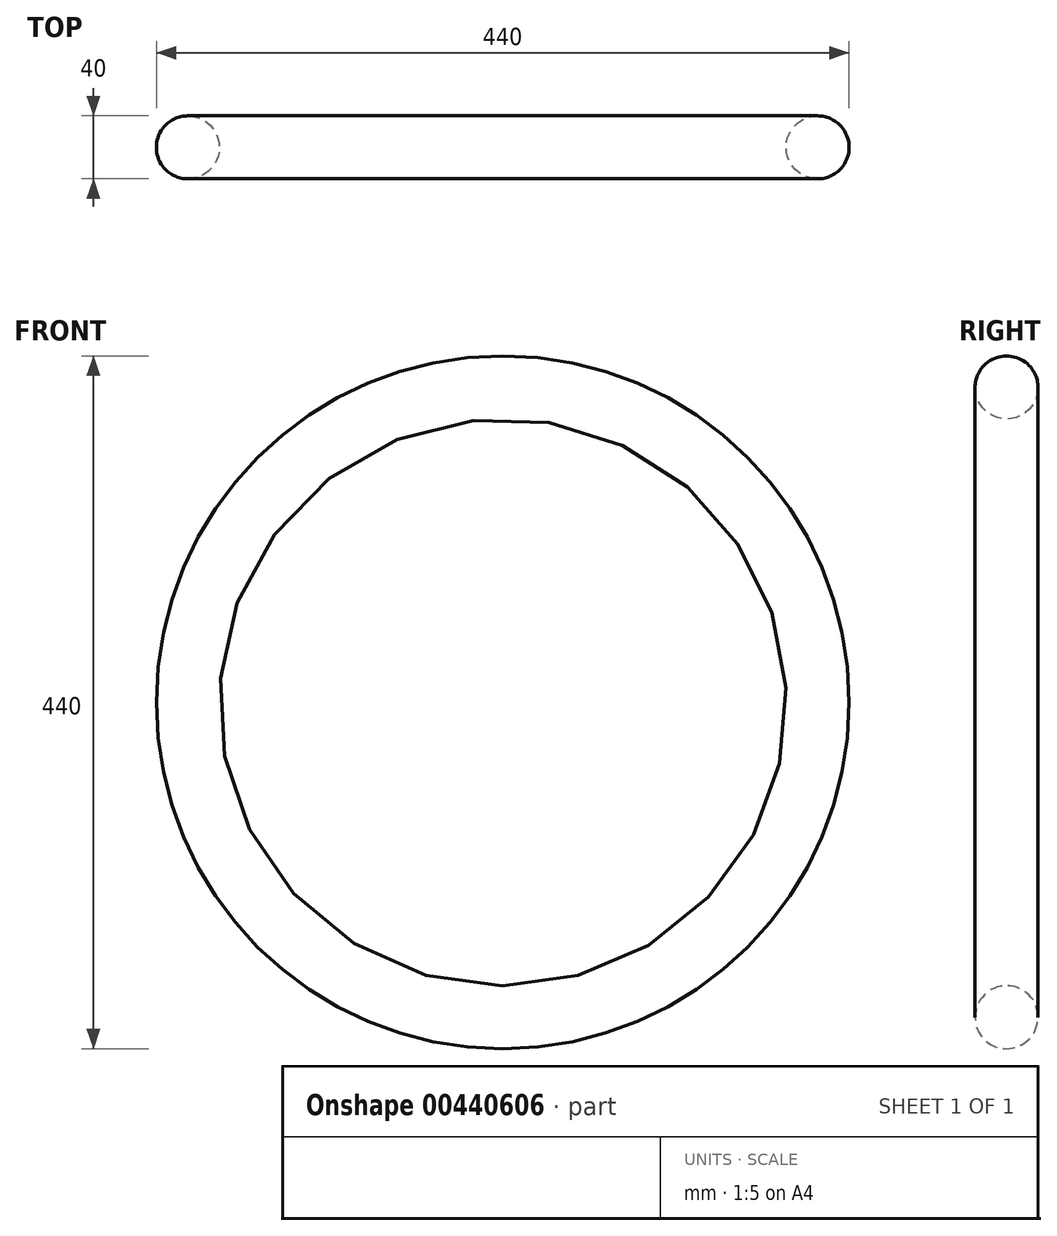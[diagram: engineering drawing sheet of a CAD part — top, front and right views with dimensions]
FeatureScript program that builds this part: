
annotation { "Feature Type Name" : "Feature", "Feature Type Description" : "" }
export const myFeature = defineFeature(function(context is Context, id is Id, definition is map)
    precondition{}
    {
        {
            var Q0;
            Q0=qCreatedBy(makeId("Right.planeOp"),FACE);
            var sketch = newSketch(context, id + "F0", { "sketchPlane" : qUnion([Q0])});
            skCircle(sketch, "E0", {"center": v(0, 200) * mm, "radius": 20 * mm});
            skLineSegment(sketch, "E1", {"start": v(-110.5, 0) * mm, "end": v(111.22, 0) * mm, "construction": true});
            skSolve(sketch);
        }
        {
            var Q0;
            Q0=makeQuery(id+"F0.imprint","IMPRINT",FACE,{"disambiguationData":[TD([[makeQuery(id+"F0.imprint","IMPRINT",EDGE,{"derivedFrom":sQuery(id+"F0.wireOp",EDGE,"E0")}),1.0]])]});
            var Q1;
            Q1=sQuery(id+"F0.wireOp",EDGE,"E0");
            var Q2;
            Q2=sQuery(id+"F0.wireOp",EDGE,"E1");
            revolve(context, id + "F1", {"entities" : qUnion([Q0]), "surfaceEntities" : qUnion([Q1]), "axis" : qUnion([Q2]), "revolveType" : RevolveType.FULL});
        }
    });
